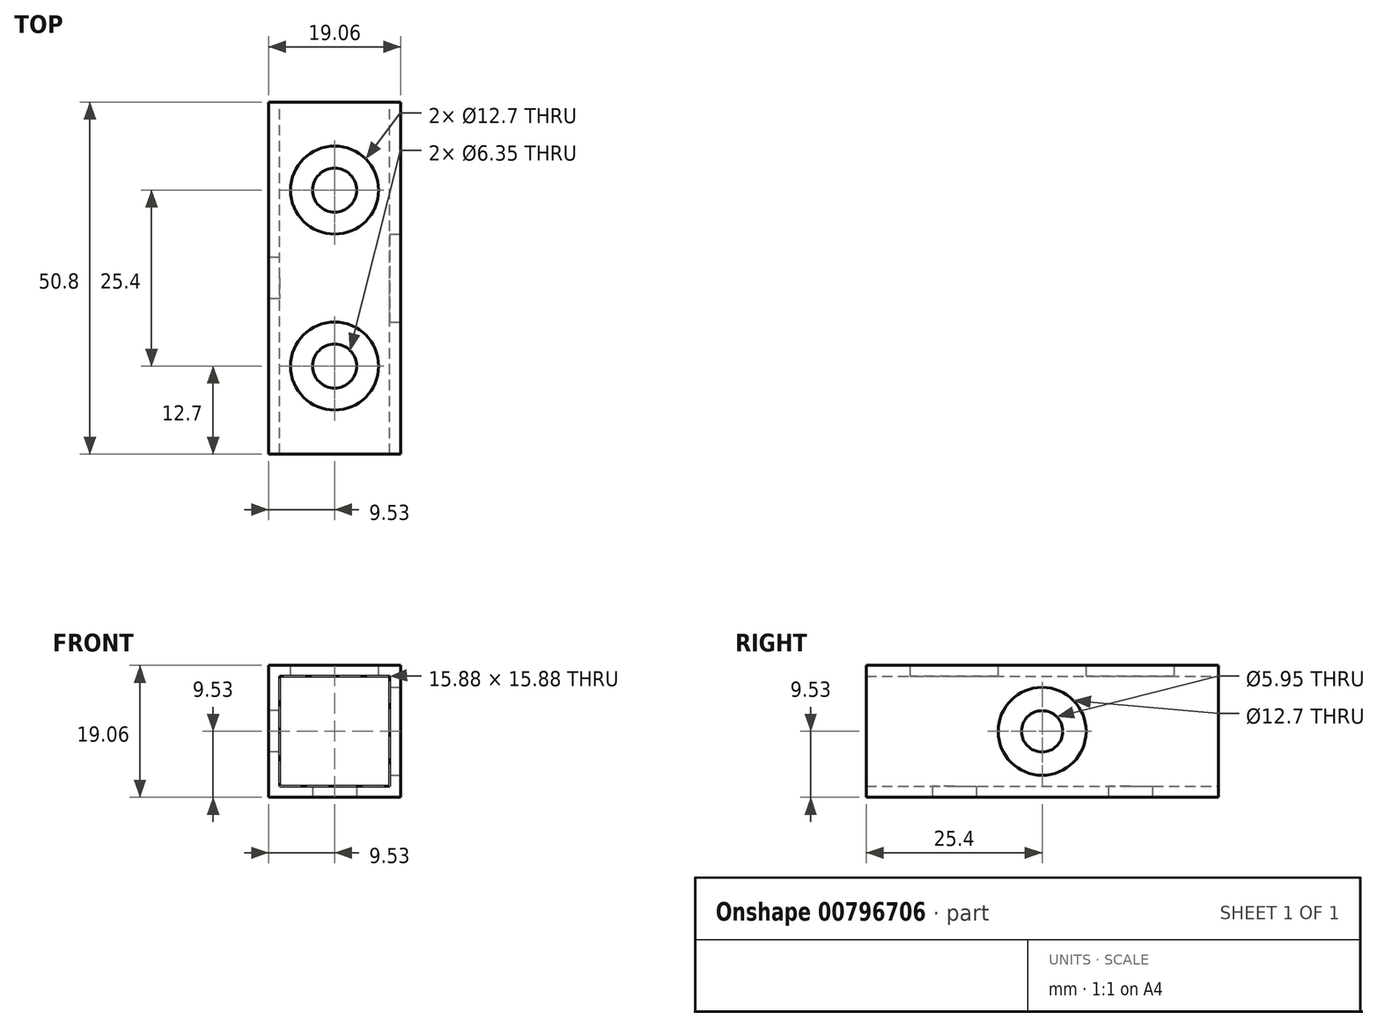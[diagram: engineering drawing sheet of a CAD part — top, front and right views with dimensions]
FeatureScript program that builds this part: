
annotation { "Feature Type Name" : "Feature", "Feature Type Description" : "" }
export const myFeature = defineFeature(function(context is Context, id is Id, definition is map)
    precondition{}
    {
        {
            var Q0;
            Q0=qCreatedBy(makeId("Front.planeOp"),FACE);
            var sketch = newSketch(context, id + "F0", { "sketchPlane" : qUnion([Q0])});
            skLineSegment(sketch, "E0.bottom", {"start": v(-9.52, 9.53) * mm, "end": v(9.53, 9.53) * mm});
            skLineSegment(sketch, "E0.top", {"start": v(-9.53, -9.53) * mm, "end": v(9.52, -9.53) * mm});
            skLineSegment(sketch, "E0.left", {"start": v(-9.52, 9.53) * mm, "end": v(-9.53, -9.52) * mm});
            skLineSegment(sketch, "E0.right", {"start": v(9.53, 9.53) * mm, "end": v(9.52, -9.52) * mm});
            skPoint(sketch, "E0.middle", {"position": v(0, 0) * mm});
            skLineSegment(sketch, "E1.bottom", {"start": v(-7.94, 7.94) * mm, "end": v(7.94, 7.94) * mm});
            skLineSegment(sketch, "E1.top", {"start": v(-7.94, -7.94) * mm, "end": v(7.94, -7.94) * mm});
            skLineSegment(sketch, "E1.left", {"start": v(-7.94, 7.94) * mm, "end": v(-7.94, -7.94) * mm});
            skLineSegment(sketch, "E1.right", {"start": v(7.94, 7.94) * mm, "end": v(7.94, -7.94) * mm});
            skSolve(sketch);
        }
        {
            var Q0;
            Q0=qSketchRegion(id+"F0",true);
            extrude(context, id + "F1", {"entities" : qUnion([Q0]), "depth" : 50.8 * mm, "offsetDistance" : 25.4 * mm});
        }
        {
            var Q0;
            Q0=makeQuery(id+"F1.opExtrude","SWEPT_FACE",FACE,{"disambiguationData":[OSD([sQuery(id+"F0.wireOp",EDGE,"E0.left")])]});
            var sketch = newSketch(context, id + "F2", { "sketchPlane" : qUnion([Q0])});
            skPoint(sketch, "E2", {"position": v(25.4, 0) * mm});
            skSolve(sketch);
        }
        {
            var Q0;
            Q0=sQuery(id+"F2.wireOp",VERTEX,"E2");
            var Q1;
            Q1=makeQuery(id+"F1.opExtrude","SWEPT_BODY",BODY,{"disambiguationData":[OSD([sQuery(id+"F0.wireOp",EDGE,"E0.bottom"),sQuery(id+"F0.wireOp",EDGE,"E0.top"),sQuery(id+"F0.wireOp",EDGE,"E0.left"),sQuery(id+"F0.wireOp",EDGE,"E0.right"),sQuery(id+"F0.wireOp",EDGE,"E1.bottom"),sQuery(id+"F0.wireOp",EDGE,"E1.top"),sQuery(id+"F0.wireOp",EDGE,"E1.left"),sQuery(id+"F0.wireOp",EDGE,"E1.right")])]});
            hole(context, id + "F3", {"style" : HoleStyle.SIMPLE, "endStyle" : HoleEndStyle.BLIND, "holeDiameter" : 5.95 * mm, "majorDiameter" : 6.35 * mm, "holeDepth" : 6.35 * mm, "isTappedThrough" : true, "tappedDepth" : 12.7 * mm, "tapClearance" : 3, "startFromSketch" : true, "locations" : qUnion([Q0]), "scope" : qUnion([Q1])});
        }
        {
            var Q0;
            Q0=makeQuery(id+"F1.opExtrude","SWEPT_FACE",FACE,{"disambiguationData":[OSD([sQuery(id+"F0.wireOp",EDGE,"E0.right")])]});
            var sketch = newSketch(context, id + "F4", { "sketchPlane" : qUnion([Q0])});
            skPoint(sketch, "E3", {"position": v(-25.4, 0) * mm});
            skSolve(sketch);
        }
        {
            var Q0;
            Q0=sQuery(id+"F4.wireOp",VERTEX,"E3");
            var Q1;
            Q1=makeQuery(id+"F1.opExtrude","SWEPT_BODY",BODY,{"disambiguationData":[OSD([sQuery(id+"F0.wireOp",EDGE,"E0.bottom"),sQuery(id+"F0.wireOp",EDGE,"E0.top"),sQuery(id+"F0.wireOp",EDGE,"E0.left"),sQuery(id+"F0.wireOp",EDGE,"E0.right"),sQuery(id+"F0.wireOp",EDGE,"E1.bottom"),sQuery(id+"F0.wireOp",EDGE,"E1.top"),sQuery(id+"F0.wireOp",EDGE,"E1.left"),sQuery(id+"F0.wireOp",EDGE,"E1.right")])]});
            hole(context, id + "F5", {"style" : HoleStyle.SIMPLE, "endStyle" : HoleEndStyle.BLIND, "holeDiameter" : 12.7 * mm, "majorDiameter" : 6.35 * mm, "holeDepth" : 6.35 * mm, "isTappedThrough" : true, "tappedDepth" : 12.7 * mm, "tapClearance" : 3, "startFromSketch" : true, "locations" : qUnion([Q0]), "scope" : qUnion([Q1])});
        }
        {
            var Q0;
            Q0=makeQuery(id+"F1.opExtrude","SWEPT_FACE",FACE,{"disambiguationData":[OSD([sQuery(id+"F0.wireOp",EDGE,"E0.bottom")])]});
            var sketch = newSketch(context, id + "F6", { "sketchPlane" : qUnion([Q0])});
            skPoint(sketch, "E4", {"position": v(0, -12.7) * mm});
            skPoint(sketch, "E5", {"position": v(0, -38.1) * mm});
            skSolve(sketch);
        }
        {
            var Q0;
            Q0=sQuery(id+"F6.wireOp",VERTEX,"E4");
            var Q1;
            Q1=sQuery(id+"F6.wireOp",VERTEX,"E5");
            var Q2;
            Q2=makeQuery(id+"F1.opExtrude","SWEPT_BODY",BODY,{"disambiguationData":[OSD([sQuery(id+"F0.wireOp",EDGE,"E0.bottom"),sQuery(id+"F0.wireOp",EDGE,"E0.top"),sQuery(id+"F0.wireOp",EDGE,"E0.left"),sQuery(id+"F0.wireOp",EDGE,"E0.right"),sQuery(id+"F0.wireOp",EDGE,"E1.bottom"),sQuery(id+"F0.wireOp",EDGE,"E1.top"),sQuery(id+"F0.wireOp",EDGE,"E1.left"),sQuery(id+"F0.wireOp",EDGE,"E1.right")])]});
            hole(context, id + "F7", {"style" : HoleStyle.SIMPLE, "endStyle" : HoleEndStyle.BLIND, "holeDiameter" : 12.7 * mm, "majorDiameter" : 6.35 * mm, "holeDepth" : 6.35 * mm, "isTappedThrough" : true, "tappedDepth" : 12.7 * mm, "tapClearance" : 3, "startFromSketch" : true, "locations" : qUnion([Q0, Q1]), "scope" : qUnion([Q2])});
        }
        {
            var Q0;
            Q0=makeQuery(id+"F1.opExtrude","SWEPT_FACE",FACE,{"disambiguationData":[OSD([sQuery(id+"F0.wireOp",EDGE,"E0.top")])]});
            var sketch = newSketch(context, id + "F8", { "sketchPlane" : qUnion([Q0])});
            skPoint(sketch, "E6", {"position": v(0, 12.7) * mm});
            skPoint(sketch, "E7", {"position": v(0, 38.1) * mm});
            skSolve(sketch);
        }
        {
            var Q0;
            Q0=sQuery(id+"F8.wireOp",VERTEX,"E6");
            var Q1;
            Q1=sQuery(id+"F8.wireOp",VERTEX,"E7");
            var Q2;
            Q2=makeQuery(id+"F1.opExtrude","SWEPT_BODY",BODY,{"disambiguationData":[OSD([sQuery(id+"F0.wireOp",EDGE,"E0.bottom"),sQuery(id+"F0.wireOp",EDGE,"E0.top"),sQuery(id+"F0.wireOp",EDGE,"E0.left"),sQuery(id+"F0.wireOp",EDGE,"E0.right"),sQuery(id+"F0.wireOp",EDGE,"E1.bottom"),sQuery(id+"F0.wireOp",EDGE,"E1.top"),sQuery(id+"F0.wireOp",EDGE,"E1.left"),sQuery(id+"F0.wireOp",EDGE,"E1.right")])]});
            hole(context, id + "F9", {"style" : HoleStyle.SIMPLE, "endStyle" : HoleEndStyle.BLIND, "holeDiameter" : 6.35 * mm, "majorDiameter" : 6.35 * mm, "holeDepth" : 6.35 * mm, "isTappedThrough" : true, "tappedDepth" : 12.7 * mm, "tapClearance" : 3, "startFromSketch" : true, "locations" : qUnion([Q0, Q1]), "scope" : qUnion([Q2])});
        }
    });
